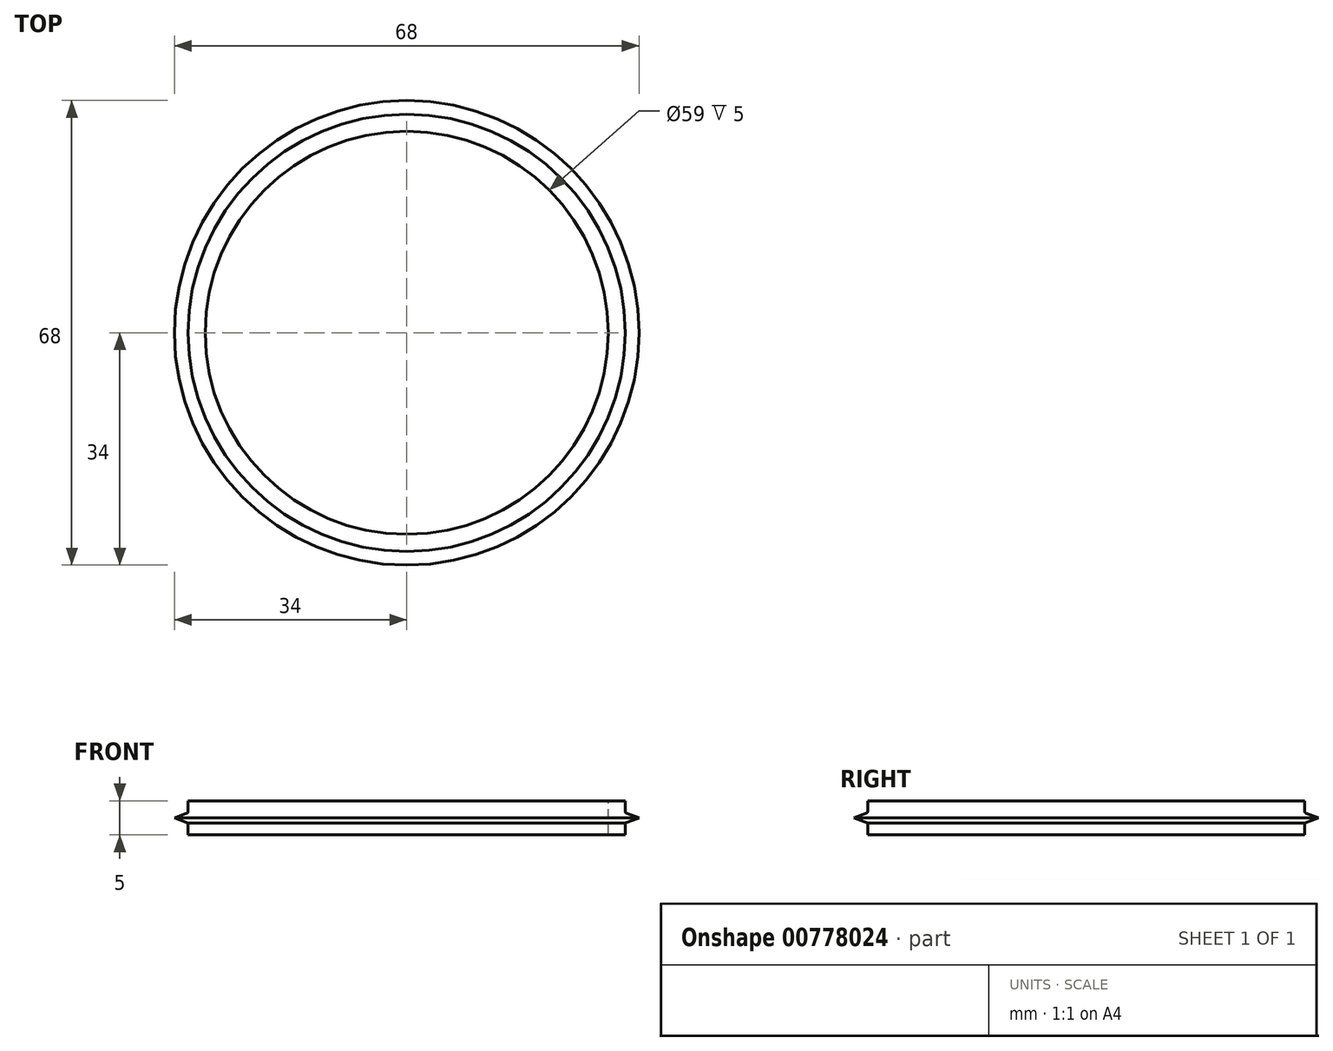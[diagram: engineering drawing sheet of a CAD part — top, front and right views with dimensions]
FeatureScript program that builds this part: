
annotation { "Feature Type Name" : "Feature", "Feature Type Description" : "" }
export const myFeature = defineFeature(function(context is Context, id is Id, definition is map)
    precondition{}
    {
        {
            var Q0;
            Q0=qCreatedBy(makeId("Top.planeOp"),FACE);
            var sketch = newSketch(context, id + "F0", { "sketchPlane" : qUnion([Q0])});
            skCircle(sketch, "E0", {"center": v(0, 0) * mm, "radius": 29.5 * mm, "construction": true});
            skLineSegment(sketch, "E1", {"start": v(-33.64, 0) * mm, "end": v(34.6, 0) * mm, "construction": true});
            skLineSegment(sketch, "E2", {"start": v(0, 35.55) * mm, "end": v(0, -35.81) * mm, "construction": true});
            skCircle(sketch, "E3", {"center": v(0, 0) * mm, "radius": 32 * mm, "construction": true});
            skCircle(sketch, "E4", {"center": v(0, 0) * mm, "radius": 34 * mm, "construction": true});
            skSolve(sketch);
        }
        {
            var Q0;
            Q0=qCreatedBy(makeId("Right.planeOp"),FACE);
            var sketch = newSketch(context, id + "F1", { "sketchPlane" : qUnion([Q0])});
            skLineSegment(sketch, "E5", {"start": v(0, 14.77) * mm, "end": v(0, -14.33) * mm, "construction": true});
            skLineSegment(sketch, "E6.bottom", {"start": v(-29.5, 2.5) * mm, "end": v(-32, 2.5) * mm});
            skLineSegment(sketch, "E6.top", {"start": v(-29.5, -2.5) * mm, "end": v(-32, -2.5) * mm});
            skLineSegment(sketch, "E6.left", {"start": v(-29.5, 2.5) * mm, "end": v(-29.5, -2.5) * mm});
            skLineSegment(sketch, "E6.right", {"start": v(-32, 2.5) * mm, "end": v(-32, -2.5) * mm});
            skLineSegment(sketch, "E7", {"start": v(-32, 0.75) * mm, "end": v(-34, 0) * mm});
            skLineSegment(sketch, "E8.MirrorCS", {"start": v(-32, -0.75) * mm, "end": v(-34, 0) * mm});
            skPoint(sketch, "E9", {"position": v(-29.5, 0) * mm});
            skSolve(sketch);
        }
        {
            var Q0;
            {var subQ1=sQuery(id+"F1.wireOp",EDGE,"E6.bottom");Q0=makeQuery(id+"F1.imprint","IMPRINT",FACE,{"disambiguationData":[TD([[makeQuery(id+"F1.imprint","IMPRINT",EDGE,{"derivedFrom":subQ1}),1.0]])]});}
            var Q1;
            {var subQ0=sQuery(id+"F1.wireOp",EDGE,"E7");Q1=makeQuery(id+"F1.imprint","IMPRINT",FACE,{"disambiguationData":[TD([[makeQuery(id+"F1.imprint","IMPRINT",EDGE,{"derivedFrom":subQ0}),1.0]])]});}
            var Q2;
            Q2=sQuery(id+"F1.wireOp",EDGE,"E5");
            revolve(context, id + "F2", {"surfaceOperationType" : NewSurfaceOperationType.NEW, "entities" : qUnion([Q0, Q1]), "axis" : qUnion([Q2]), "revolveType" : RevolveType.FULL});
        }
        {
            var Q0;
            Q0=makeQuery(id+"F2.opRevolve","SWEPT_EDGE",EDGE,{"disambiguationData":[OSD([sQuery(id+"F1.wireOp",EDGE,"E6.right"),sQuery(id+"F1.wireOp",EDGE,"E7")])]});
            fillet(context, id + "F3", {"entities" : qUnion([Q0]), "radius" : .2 * mm, "tangentPropagation" : true, "allowEdgeOverflow" : false});
        }
    });
